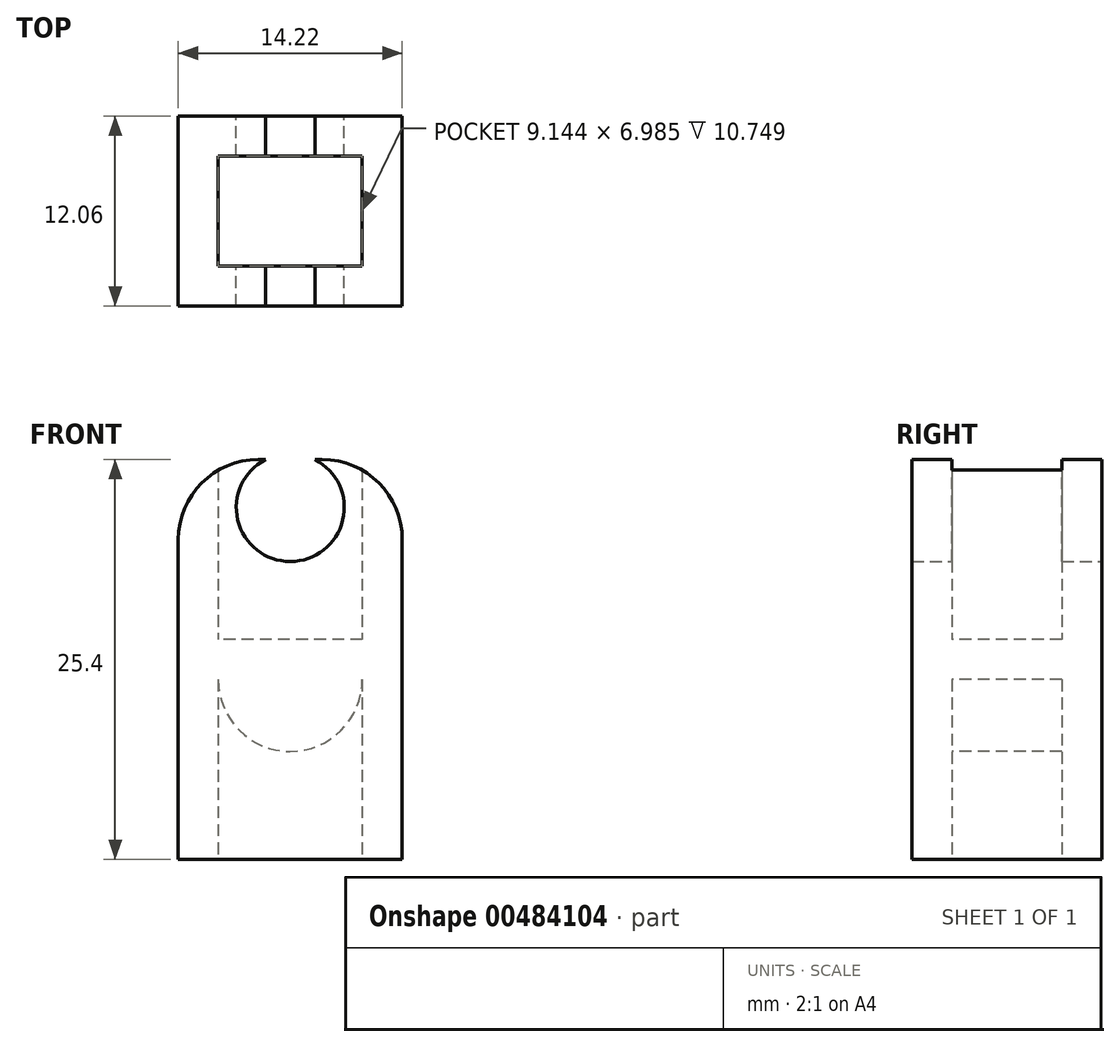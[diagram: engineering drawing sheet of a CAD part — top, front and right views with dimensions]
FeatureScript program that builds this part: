
annotation { "Feature Type Name" : "Feature", "Feature Type Description" : "" }
export const myFeature = defineFeature(function(context is Context, id is Id, definition is map)
    precondition{}
    {
        {
            var Q0;
            Q0=qCreatedBy(makeId("Top.planeOp"),FACE);
            var sketch = newSketch(context, id + "F0", { "sketchPlane" : qUnion([Q0])});
            skLineSegment(sketch, "E0.bottom", {"start": v(4.57, -3.5) * mm, "end": v(-4.57, -3.5) * mm});
            skLineSegment(sketch, "E0.top", {"start": v(4.57, 3.5) * mm, "end": v(-4.57, 3.5) * mm});
            skLineSegment(sketch, "E0.left", {"start": v(4.57, -3.5) * mm, "end": v(4.57, 3.5) * mm});
            skLineSegment(sketch, "E0.right", {"start": v(-4.57, -3.5) * mm, "end": v(-4.57, 3.5) * mm});
            skPoint(sketch, "E0.middle", {"position": v(0, 0) * mm});
            skLineSegment(sketch, "E1.bottom", {"start": v(7.11, -6.03) * mm, "end": v(-7.11, -6.03) * mm});
            skLineSegment(sketch, "E1.top", {"start": v(7.11, 6.03) * mm, "end": v(-7.11, 6.03) * mm});
            skLineSegment(sketch, "E1.left", {"start": v(7.11, -6.03) * mm, "end": v(7.11, 6.03) * mm});
            skLineSegment(sketch, "E1.right", {"start": v(-7.11, -6.03) * mm, "end": v(-7.11, 6.03) * mm});
            skSolve(sketch);
        }
        {
            var Q0;
            Q0=makeQuery(id+"F0.imprint","IMPRINT",FACE,{"disambiguationData":[TD([[makeQuery(id+"F0.imprint","IMPRINT",EDGE,{"derivedFrom":sQuery(id+"F0.wireOp",EDGE,"E0.bottom")}),1.0]])]});
            extrude(context, id + "F1", {"entities" : qUnion([Q0]), "depth" : 25.4 * mm});
        }
        {
            var Q0;
            Q0=makeQuery(id+"F1.opExtrude","SWEPT_FACE",FACE,{"disambiguationData":[OSD([sQuery(id+"F0.wireOp",EDGE,"E0.bottom")])]});
            var sketch = newSketch(context, id + "F2", { "sketchPlane" : qUnion([Q0])});
            skLineSegment(sketch, "E2.bottom", {"start": v(-4.57, 13.97) * mm, "end": v(4.57, 13.97) * mm});
            skLineSegment(sketch, "E2.top", {"start": v(-4.57, 11.43) * mm, "end": v(4.57, 11.43) * mm});
            skLineSegment(sketch, "E2.left", {"start": v(-4.57, 13.97) * mm, "end": v(-4.57, 11.43) * mm});
            skLineSegment(sketch, "E2.right", {"start": v(4.57, 13.97) * mm, "end": v(4.57, 11.43) * mm});
            skCircle(sketch, "E3", {"center": v(0, 11.43) * mm, "radius": 4.57 * mm});
            skSolve(sketch);
        }
        {
            var Q0;
            {var subQ4=sQuery(id+"F2.wireOp",EDGE,"E2.top");Q0=makeQuery(id+"F2.imprint","IMPRINT",FACE,{"disambiguationData":[TD([[makeQuery(id+"F2.imprint","IMPRINT",EDGE,{"derivedFrom":subQ4}),1.0]])]});}
            var Q1;
            {var subQ0=sQuery(id+"F2.wireOp",EDGE,"E2.left");Q1=makeQuery(id+"F2.imprint","IMPRINT",FACE,{"disambiguationData":[TD([[makeQuery(id+"F2.imprint","IMPRINT",EDGE,{"derivedFrom":subQ0}),1.0]])]});}
            var Q2;
            {var subQ0=sQuery(id+"F2.wireOp",EDGE,"E2.right");Q2=makeQuery(id+"F2.imprint","IMPRINT",FACE,{"disambiguationData":[TD([[makeQuery(id+"F2.imprint","IMPRINT",EDGE,{"derivedFrom":subQ0}),-1.0]])]});}
            var Q3;
            {var subQ0=sQuery(id+"F2.wireOp",EDGE,"E2.top");Q3=makeQuery(id+"F2.imprint","IMPRINT",FACE,{"disambiguationData":[TD([[makeQuery(id+"F2.imprint","IMPRINT",EDGE,{"derivedFrom":subQ0}),-1.0]])]});}
            extrude(context, id + "F3", {"entities" : qUnion([Q0, Q1, Q2, Q3]), "operationType" : NewBodyOperationType.ADD, "depth" : 8.9 * mm});
        }
        {
            var Q0;
            Q0=makeQuery(id+"F1.opExtrude","SWEPT_FACE",FACE,{"disambiguationData":[OSD([sQuery(id+"F0.wireOp",EDGE,"E1.top")])]});
            var sketch = newSketch(context, id + "F4", { "sketchPlane" : qUnion([Q0])});
            skCircle(sketch, "E4", {"center": v(0, 22.35) * mm, "radius": 3.43 * mm});
            skSolve(sketch);
        }
        {
            var Q0;
            {var subQ0=sQuery(id+"F4.wireOp",EDGE,"E4");var subQ1=makeQuery(id+"F1.opExtrude","CAP_EDGE",EDGE,{"disambiguationData":[OSD([sQuery(id+"F0.wireOp",EDGE,"E1.top")])],"isStart":false});var subQ2=makeQuery(id+"F4.imprint","INTERSECT",VERTEX,{"disambiguationData":[OD(0.0)],"derivedFrom":[subQ1,subQ0]});Q0=makeQuery(id+"F4.imprint","IMPRINT",FACE,{"disambiguationData":[TD([[makeQuery(id+"F4.imprint","IMPRINT",EDGE,{"disambiguationData":[TD([[subQ2,-1.0]])],"derivedFrom":subQ0}),1.0]])]});}
            extrude(context, id + "F5", {"entities" : qUnion([Q0]), "operationType" : NewBodyOperationType.REMOVE, "oppositeDirection" : true, "depth" : 25.4 * mm});
        }
        {
            var Q0;
            Q0=makeQuery(id+"F1.opExtrude","CAP_EDGE",EDGE,{"disambiguationData":[OSD([sQuery(id+"F0.wireOp",EDGE,"E1.left")])],"isStart":false});
            var Q1;
            Q1=makeQuery(id+"F1.opExtrude","CAP_EDGE",EDGE,{"disambiguationData":[OSD([sQuery(id+"F0.wireOp",EDGE,"E1.right")])],"isStart":false});
            fillet(context, id + "F6", {"entities" : qUnion([Q0, Q1]), "radius" : 5.08 * mm, "tangentPropagation" : true, "allowEdgeOverflow" : false});
        }
    });
